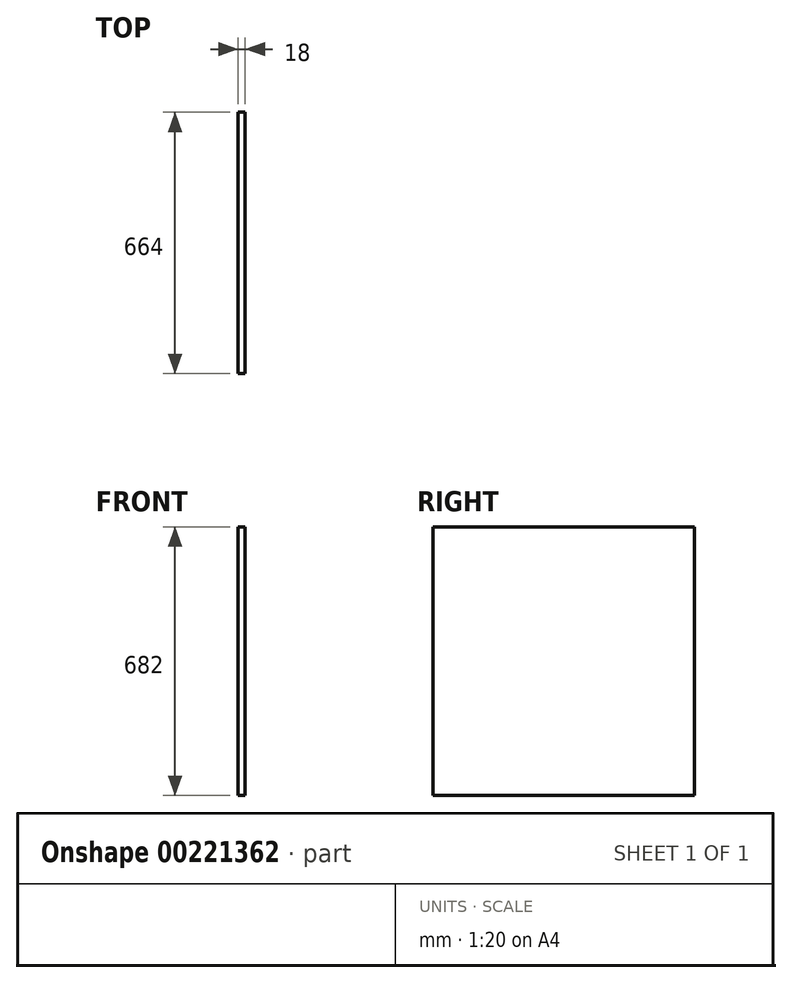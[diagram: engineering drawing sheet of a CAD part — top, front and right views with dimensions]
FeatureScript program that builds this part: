
annotation { "Feature Type Name" : "Feature", "Feature Type Description" : "" }
export const myFeature = defineFeature(function(context is Context, id is Id, definition is map)
    precondition{}
    {
        {
            var Q0;
            Q0=qCreatedBy(makeId("Right.planeOp"),FACE);
            var sketch = newSketch(context, id + "F0", { "sketchPlane" : qUnion([Q0])});
            skLineSegment(sketch, "E0.bottom", {"start": v(332, -341) * mm, "end": v(-332, -341) * mm});
            skLineSegment(sketch, "E0.top", {"start": v(332, 341) * mm, "end": v(-332, 341) * mm});
            skLineSegment(sketch, "E0.left", {"start": v(332, -341) * mm, "end": v(332, 341) * mm});
            skLineSegment(sketch, "E0.right", {"start": v(-332, -341) * mm, "end": v(-332, 341) * mm});
            skPoint(sketch, "E0.middle", {"position": v(0, 0) * mm});
            skSolve(sketch);
        }
        {
            var Q0;
            Q0 = qSketchRegion(id + "F0", true);
            extrude(context, id + "F1", {"entities" : qUnion([Q0]), "depth" : 18 * mm});
        }
    });
